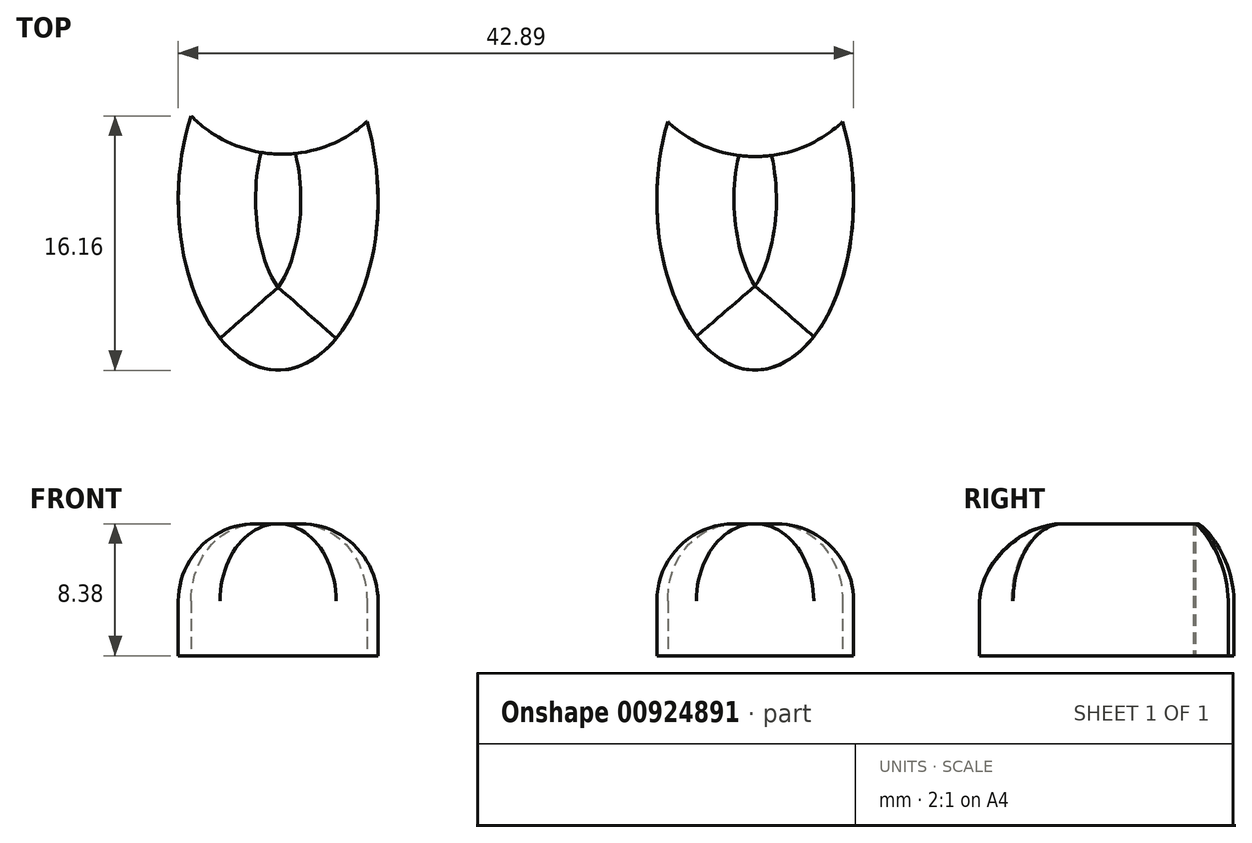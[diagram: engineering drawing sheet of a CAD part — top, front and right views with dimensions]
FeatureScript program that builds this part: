
annotation { "Feature Type Name" : "Feature", "Feature Type Description" : "" }
export const myFeature = defineFeature(function(context is Context, id is Id, definition is map)
    precondition{}
    {
        {
            var Q0;
            Q0=qCreatedBy(makeId("Top.planeOp"),FACE);
            var sketch = newSketch(context, id + "F0", { "sketchPlane" : qUnion([Q0])});
            skEllipticalArc(sketch, "E0", {});
            skEllipticalArc(sketch, "E1", {});
            skArc(sketch, "E2", {"start": v(-21.18, 5.33) * mm, "mid": v(-15.67, 2.9) * mm, "end": v(-10.02, 4.96) * mm});
            skArc(sketch, "E3", {"start": v(9.1, 4.96) * mm, "mid": v(14.64, 2.74) * mm, "end": v(20.2, 4.96) * mm});
            const initialGuessF0  = {"E0": [-0.015656854957342148, 0, 0, 1, 0.010825433768332005, 0.0063418261949640346, 1.0563309347564394, 5.1887281694498455], "E1": [0.014642789028584957, 0, 0, -1, 0.01082170195877552, 0.006247804026127486, 4.235871854642054, 2.0473134525375323]};
            skSetInitialGuess(sketch, initialGuessF0);
            skSolve(sketch);
        }
        {
            var Q0;
            Q0=makeQuery(id+"F0.imprint","IMPRINT",FACE,{"disambiguationData":[TD([[makeQuery(id+"F0.imprint","IMPRINT",EDGE,{"derivedFrom":sQuery(id+"F0.wireOp",EDGE,"E0")}),1.0]])]});
            var Q1;
            Q1=makeQuery(id+"F0.imprint","IMPRINT",FACE,{"disambiguationData":[TD([[makeQuery(id+"F0.imprint","IMPRINT",EDGE,{"derivedFrom":sQuery(id+"F0.wireOp",EDGE,"E1")}),1.0]])]});
            extrude(context, id + "F1", {"entities" : qUnion([Q0, Q1]), "depth" : 8.38 * mm, "offsetDistance" : 25.4 * mm});
        }
        {
            var Q0;
            Q0=makeQuery(id+"F1.opExtrude","CAP_EDGE",EDGE,{"disambiguationData":[OSD([sQuery(id+"F0.wireOp",EDGE,"E0")])],"isStart":false});
            var Q1;
            Q1=makeQuery(id+"F1.opExtrude","CAP_EDGE",EDGE,{"disambiguationData":[OSD([sQuery(id+"F0.wireOp",EDGE,"E1")])],"isStart":false});
            fillet(context, id + "F2", {"entities" : qUnion([Q0, Q1]), "radius" : 4.9 * mm, "tangentPropagation" : true, "allowEdgeOverflow" : false});
        }
    });
